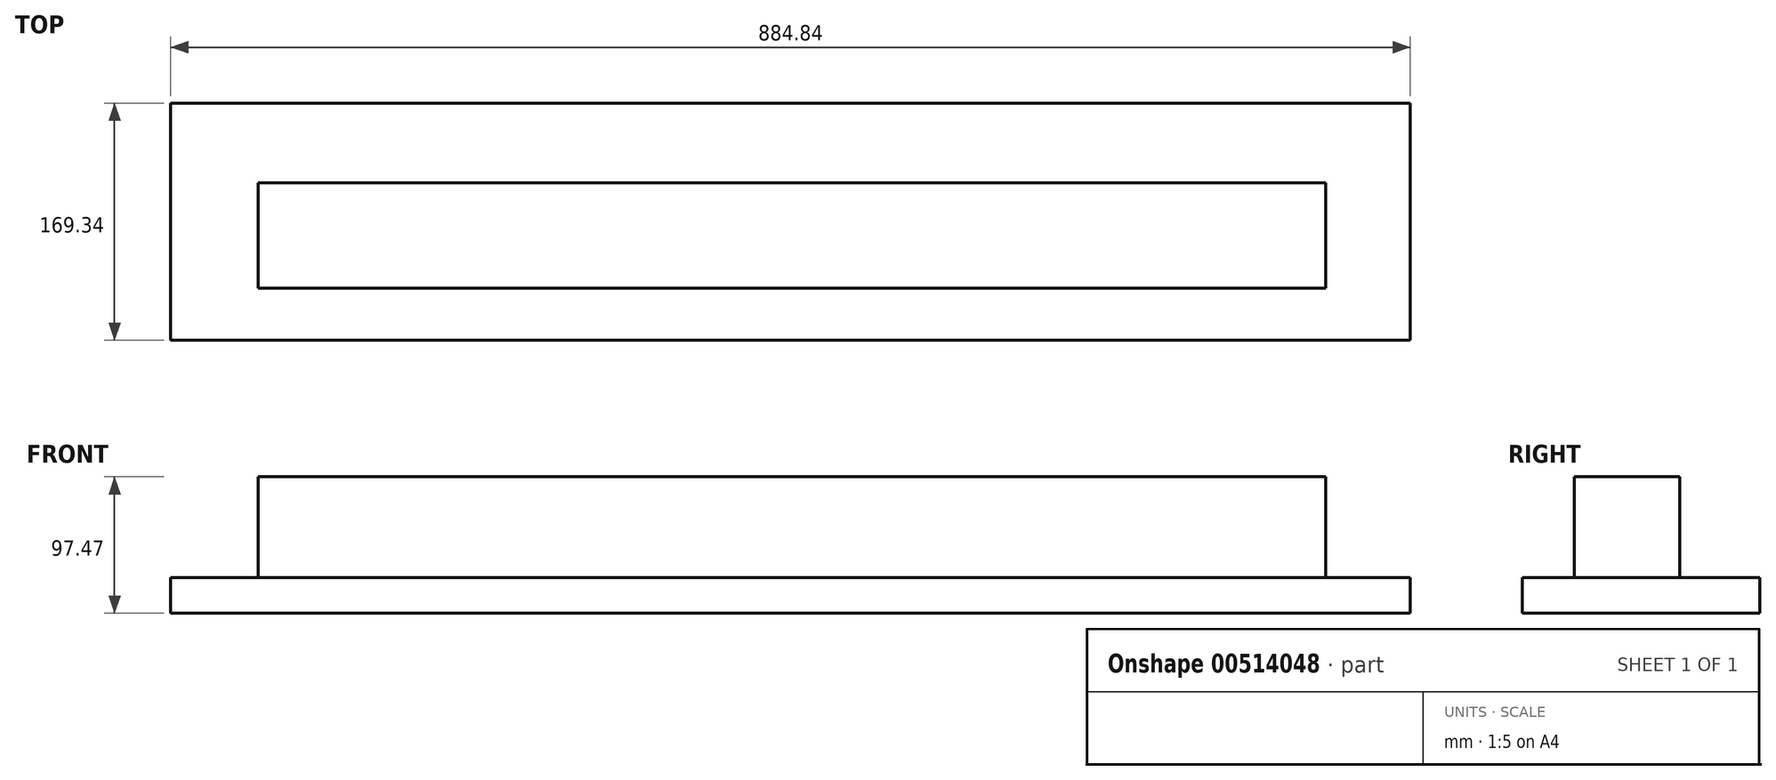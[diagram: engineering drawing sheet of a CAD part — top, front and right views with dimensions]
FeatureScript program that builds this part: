
annotation { "Feature Type Name" : "Feature", "Feature Type Description" : "" }
export const myFeature = defineFeature(function(context is Context, id is Id, definition is map)
    precondition{}
    {
        {
            var Q0;
            Q0=qCreatedBy(makeId("Right.planeOp"),FACE);
            var sketch = newSketch(context, id + "F0", { "sketchPlane" : qUnion([Q0])});
            skLineSegment(sketch, "E0.bottom", {"start": v(-32.89, -36.22) * mm, "end": v(42.5, -36.22) * mm});
            skLineSegment(sketch, "E0.top", {"start": v(-32.89, 35.85) * mm, "end": v(42.5, 35.85) * mm});
            skLineSegment(sketch, "E0.left", {"start": v(-32.89, -36.22) * mm, "end": v(-32.89, 35.85) * mm});
            skLineSegment(sketch, "E0.right", {"start": v(42.5, -36.22) * mm, "end": v(42.5, 35.85) * mm});
            skSolve(sketch);
        }
        {
            var Q0;
            Q0 = qSketchRegion(id + "F0", true);
            extrude(context, id + "F1", {"entities" : qUnion([Q0]), "endBound" : BoundingType.SYMMETRIC, "depth" : 762 * mm});
        }
        {
            var Q0;
            Q0=makeQuery(id+"F1.opExtrude","SWEPT_FACE",FACE,{"disambiguationData":[OSD([sQuery(id+"F0.wireOp",EDGE,"E0.bottom")])]});
            var sketch = newSketch(context, id + "F2", { "sketchPlane" : qUnion([Q0])});
            skLineSegment(sketch, "E1.bottom", {"start": v(-443.5, 69.95) * mm, "end": v(441.35, 69.95) * mm});
            skLineSegment(sketch, "E1.top", {"start": v(-443.5, -99.4) * mm, "end": v(441.35, -99.4) * mm});
            skLineSegment(sketch, "E1.left", {"start": v(-443.5, 69.95) * mm, "end": v(-443.5, -99.4) * mm});
            skLineSegment(sketch, "E1.right", {"start": v(441.35, 69.95) * mm, "end": v(441.35, -99.4) * mm});
            skSolve(sketch);
        }
        {
            var Q0;
            Q0 = qSketchRegion(id + "F2", true);
            extrude(context, id + "F3", {"entities" : qUnion([Q0]), "operationType" : NewBodyOperationType.ADD, "depth" : 25.4 * mm});
        }
    });
